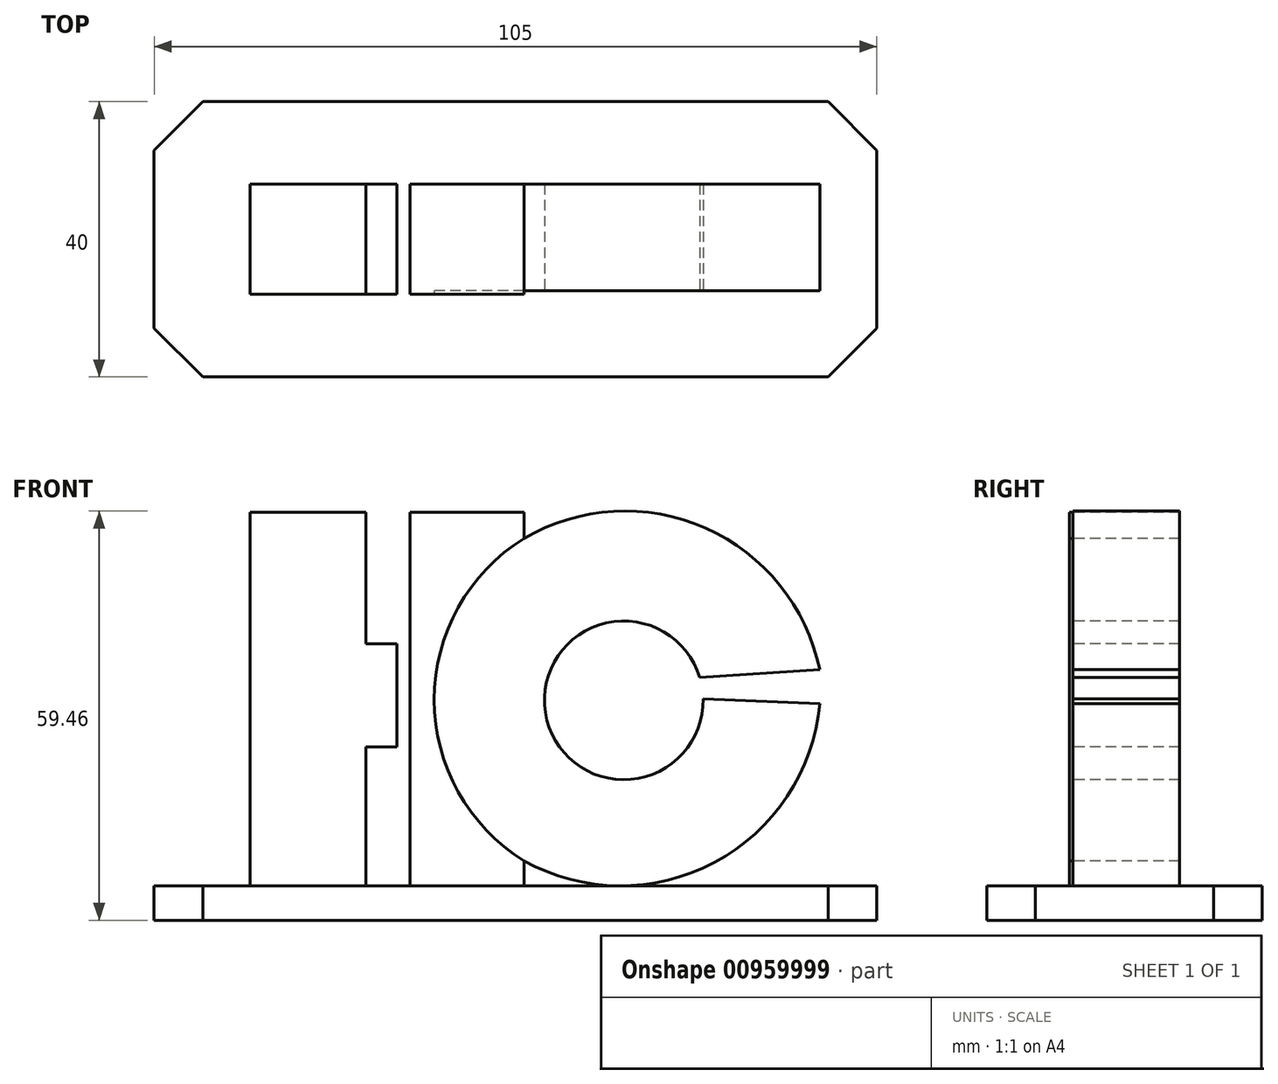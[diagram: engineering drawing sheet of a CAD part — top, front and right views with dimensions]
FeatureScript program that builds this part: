
annotation { "Feature Type Name" : "Feature", "Feature Type Description" : "" }
export const myFeature = defineFeature(function(context is Context, id is Id, definition is map)
    precondition{}
    {
        {
            var Q0;
            Q0=qCreatedBy(makeId("Front.planeOp"),FACE);
            var sketch = newSketch(context, id + "F0", { "sketchPlane" : qUnion([Q0])});
            skLineSegment(sketch, "E0.bottom", {"start": v(0, 0) * mm, "end": v(16.8, 0) * mm});
            skLineSegment(sketch, "E0.top", {"start": v(0, 54.3) * mm, "end": v(16.8, 54.3) * mm});
            skLineSegment(sketch, "E0.left", {"start": v(0, 0) * mm, "end": v(0, 54.3) * mm});
            skLineSegment(sketch, "E0.right", {"start": v(16.8, 0) * mm, "end": v(16.8, 20.2) * mm});
            skLineSegment(sketch, "E1.bottom", {"start": v(23.22, 54.3) * mm, "end": v(39.8, 54.3) * mm});
            skLineSegment(sketch, "E1.top", {"start": v(23.22, 0) * mm, "end": v(39.8, 0) * mm});
            skLineSegment(sketch, "E1.left", {"start": v(23.22, 54.3) * mm, "end": v(23.22, 0) * mm});
            skLineSegment(sketch, "E1.right", {"start": v(39.8, 54.3) * mm, "end": v(39.8, 50.47) * mm});
            skArc(sketch, "E2", {"start": v(65.35, 30.25) * mm, "mid": v(42.9, 25.18) * mm, "end": v(65.83, 27.15) * mm});
            skLineSegment(sketch, "E3", {"start": v(65.35, 30.25) * mm, "end": v(82.79, 31.4) * mm});
            skArc(sketch, "E4", {"start": v(82.79, 31.4) * mm, "mid": v(66.18, 51.97) * mm, "end": v(39.8, 50.47) * mm});
            skLineSegment(sketch, "E5", {"start": v(65.83, 27.15) * mm, "end": v(82.79, 26.46) * mm});
            skArc(sketch, "E6", {"start": v(39.8, 3.64) * mm, "mid": v(67.47, 3.4) * mm, "end": v(82.79, 26.46) * mm});
            skLineSegment(sketch, "E7.trimOffspring", {"start": v(39.8, 3.64) * mm, "end": v(39.8, 0) * mm});
            skLineSegment(sketch, "E8.bottom", {"start": v(16.8, 20.2) * mm, "end": v(21.33, 20.2) * mm});
            skLineSegment(sketch, "E8.top", {"start": v(16.8, 35.15) * mm, "end": v(21.33, 35.15) * mm});
            skLineSegment(sketch, "E8.right", {"start": v(21.33, 20.2) * mm, "end": v(21.33, 35.15) * mm});
            skLineSegment(sketch, "E9.trimOffspring", {"start": v(16.8, 35.15) * mm, "end": v(16.8, 54.3) * mm});
            skSolve(sketch);
        }
        {
            var Q0;
            Q0 = qSketchRegion(id + "F0", true);
            extrude(context, id + "F1", {"entities" : qUnion([Q0]), "oppositeDirection" : true, "depth" : 16 * mm, "offsetDistance" : 25 * mm});
        }
        {
            var Q0;
            Q0=qCreatedBy(makeId("Top.planeOp"),FACE);
            var sketch = newSketch(context, id + "F2", { "sketchPlane" : qUnion([Q0])});
            skLineSegment(sketch, "E10", {"start": v(0, 0) * mm, "end": v(0, 16) * mm, "construction": true});
            skLineSegment(sketch, "E11", {"start": v(0, 8) * mm, "end": v(77.11, 8) * mm, "construction": true});
            skLineSegment(sketch, "E12.bottom", {"start": v(-13.94, 28) * mm, "end": v(91.06, 28) * mm});
            skLineSegment(sketch, "E12.top", {"start": v(-13.94, -12) * mm, "end": v(91.06, -12) * mm});
            skLineSegment(sketch, "E12.left", {"start": v(-13.94, 28) * mm, "end": v(-13.94, -12) * mm});
            skLineSegment(sketch, "E12.right", {"start": v(91.06, 28) * mm, "end": v(91.06, -12) * mm});
            skPoint(sketch, "E12.middle", {"position": v(38.56, 8) * mm});
            skLineSegment(sketch, "E13", {"start": v(-13.94, 20.93) * mm, "end": v(-6.87, 28) * mm});
            skLineSegment(sketch, "E14.MirrorCS", {"start": v(-13.94, -4.93) * mm, "end": v(-6.87, -12) * mm});
            skLineSegment(sketch, "E15", {"start": v(38.56, 8) * mm, "end": v(38.56, 19.72) * mm, "construction": true});
            skLineSegment(sketch, "E16.MirrorCS", {"start": v(91.06, 20.93) * mm, "end": v(83.99, 28) * mm});
            skLineSegment(sketch, "E17.MirrorCS", {"start": v(91.06, -4.93) * mm, "end": v(83.99, -12) * mm});
            skSolve(sketch);
        }
        {
            var Q0;
            {var subQ3=sQuery(id+"F2.wireOp",EDGE,"E13");Q0=makeQuery(id+"F2.imprint","IMPRINT",FACE,{"disambiguationData":[TD([[makeQuery(id+"F2.imprint","IMPRINT",EDGE,{"derivedFrom":subQ3}),-1.0]])]});}
            extrude(context, id + "F3", {"entities" : qUnion([Q0]), "oppositeDirection" : true, "depth" : 5 * mm, "offsetDistance" : 25 * mm});
        }
        {
            var Q0;
            Q0=makeQuery(id+"F1.opExtrude","CAP_FACE",FACE,{"disambiguationData":[OSD([sQuery(id+"F0.wireOp",EDGE,"E1.bottom"),sQuery(id+"F0.wireOp",EDGE,"E1.top"),sQuery(id+"F0.wireOp",EDGE,"E1.left"),sQuery(id+"F0.wireOp",EDGE,"E1.right"),sQuery(id+"F0.wireOp",EDGE,"E2"),sQuery(id+"F0.wireOp",EDGE,"E3"),sQuery(id+"F0.wireOp",EDGE,"E4"),sQuery(id+"F0.wireOp",EDGE,"E5"),sQuery(id+"F0.wireOp",EDGE,"E6"),sQuery(id+"F0.wireOp",EDGE,"E7.trimOffspring")])],"isStart":true});
            var sketch = newSketch(context, id + "F4", { "sketchPlane" : qUnion([Q0])});
            skLineSegment(sketch, "E18.0", {"start": v(65.35, 30.25) * mm, "end": v(82.79, 31.4) * mm});
            skLineSegment(sketch, "E18.1", {"start": v(65.83, 27.15) * mm, "end": v(82.79, 26.46) * mm});
            skArc(sketch, "E18.2", {"start": v(65.35, 30.25) * mm, "mid": v(42.9, 25.18) * mm, "end": v(65.83, 27.15) * mm});
            skArc(sketch, "E19.0", {"start": v(82.79, 31.4) * mm, "mid": v(66.18, 51.97) * mm, "end": v(39.8, 50.47) * mm});
            skArc(sketch, "E20.0", {"start": v(39.8, 3.64) * mm, "mid": v(67.47, 3.4) * mm, "end": v(82.79, 26.46) * mm});
            skArc(sketch, "E21", {"start": v(39.8, 50.47) * mm, "mid": v(26.76, 27.05) * mm, "end": v(39.8, 3.64) * mm});
            skSolve(sketch);
        }
        {
            var Q0;
            Q0=makeQuery(id+"F4.imprint","IMPRINT",FACE,{"disambiguationData":[TD([[makeQuery(id+"F4.imprint","IMPRINT",EDGE,{"derivedFrom":sQuery(id+"F4.wireOp",EDGE,"E18.0")}),1.0]])]});
            extrude(context, id + "F5", {"entities" : qUnion([Q0]), "operationType" : NewBodyOperationType.REMOVE, "oppositeDirection" : true, "depth" : .5 * mm, "offsetDistance" : 25 * mm});
        }
    });
